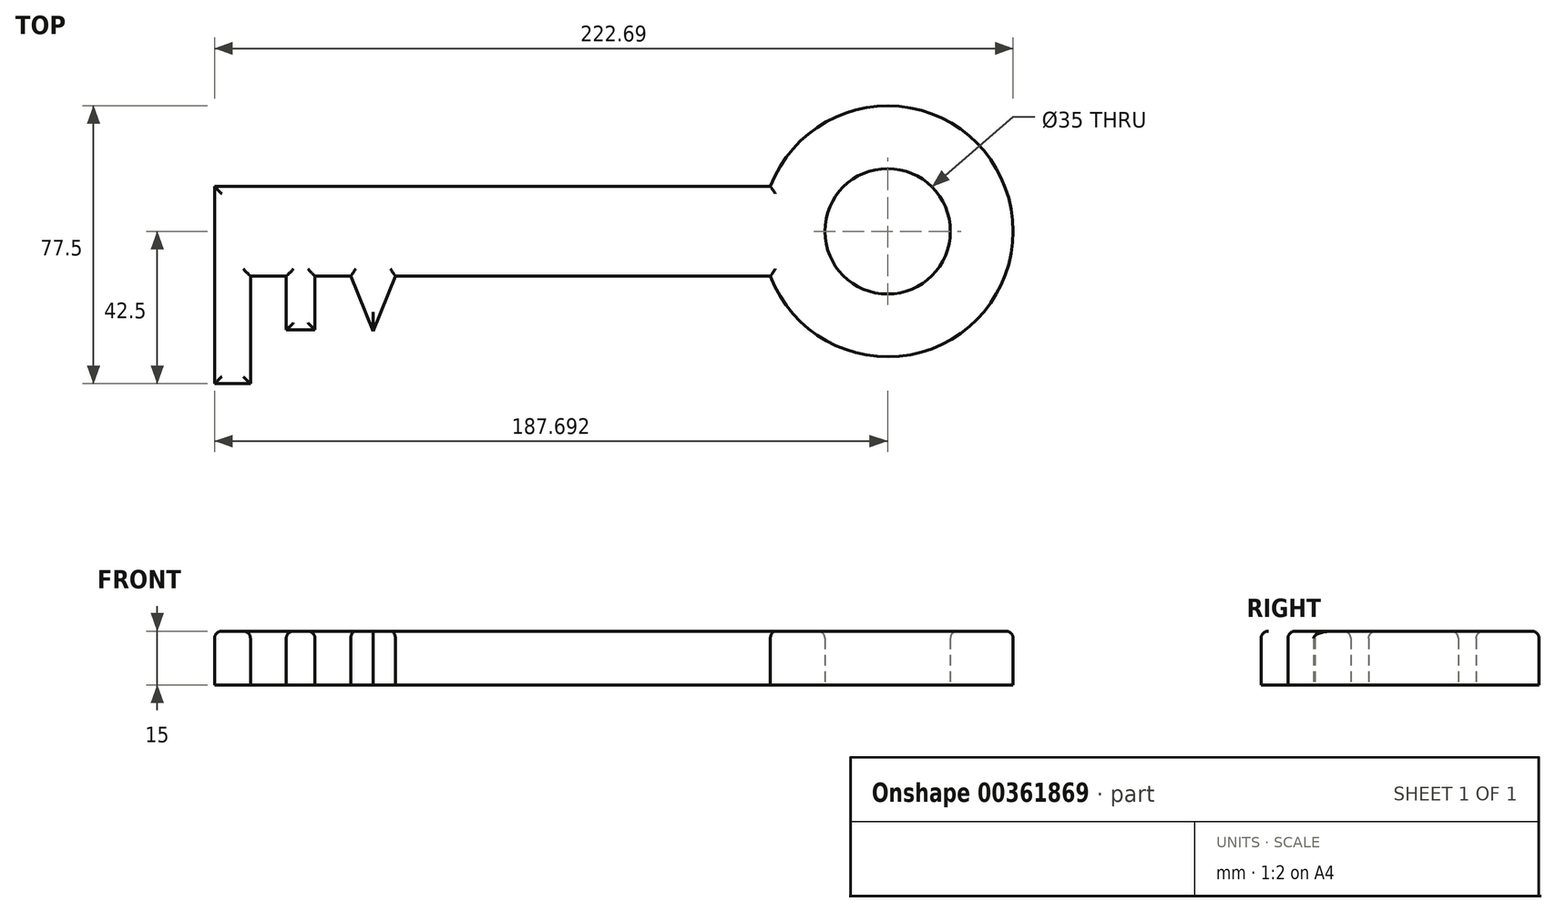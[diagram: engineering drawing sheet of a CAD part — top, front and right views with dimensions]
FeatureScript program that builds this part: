
annotation { "Feature Type Name" : "Feature", "Feature Type Description" : "" }
export const myFeature = defineFeature(function(context is Context, id is Id, definition is map)
    precondition{}
    {
        {
            var Q0;
            Q0=qCreatedBy(makeId("Top.planeOp"),FACE);
            var sketch = newSketch(context, id + "F0", { "sketchPlane" : qUnion([Q0])});
            skLineSegment(sketch, "E0.bottom", {"start": v(-84.95, 32.85) * mm, "end": v(70.05, 32.85) * mm});
            skLineSegment(sketch, "E0.top", {"start": v(-84.95, 7.85) * mm, "end": v(70.05, 7.85) * mm});
            skLineSegment(sketch, "E0.left", {"start": v(-84.95, 32.85) * mm, "end": v(-84.95, 7.85) * mm});
            skLineSegment(sketch, "E0.right", {"start": v(70.05, 32.85) * mm, "end": v(70.05, 7.85) * mm});
            skLineSegment(sketch, "E1.bottom", {"start": v(-84.95, 7.85) * mm, "end": v(-74.95, 7.85) * mm});
            skLineSegment(sketch, "E1.top", {"start": v(-84.95, -22.15) * mm, "end": v(-74.95, -22.15) * mm});
            skLineSegment(sketch, "E1.left", {"start": v(-84.95, 7.85) * mm, "end": v(-84.95, -22.15) * mm});
            skLineSegment(sketch, "E1.right", {"start": v(-74.95, 7.85) * mm, "end": v(-74.95, -22.15) * mm});
            skLineSegment(sketch, "E2.bottom", {"start": v(-64.95, 7.85) * mm, "end": v(-56.95, 7.85) * mm});
            skLineSegment(sketch, "E2.top", {"start": v(-64.95, -7.15) * mm, "end": v(-56.95, -7.15) * mm});
            skLineSegment(sketch, "E2.left", {"start": v(-64.95, 7.85) * mm, "end": v(-64.95, -7.15) * mm});
            skLineSegment(sketch, "E2.right", {"start": v(-56.95, 7.85) * mm, "end": v(-56.95, -7.15) * mm});
            skPoint(sketch, "E3", {"position": v(-46.95, 7.85) * mm});
            skPoint(sketch, "E4", {"position": v(-34.52, 7.85) * mm});
            skPoint(sketch, "E5", {"position": v(-40.74, -7.5) * mm});
            skLineSegment(sketch, "E6", {"start": v(-46.95, 7.85) * mm, "end": v(-40.74, -7.5) * mm});
            skLineSegment(sketch, "E7", {"start": v(-40.74, -7.5) * mm, "end": v(-34.52, 7.85) * mm});
            skArc(sketch, "E8", {"start": v(70.05, 7.85) * mm, "mid": v(137.74, 20.35) * mm, "end": v(70.05, 32.85) * mm});
            skCircle(sketch, "E9", {"center": v(102.74, 20.35) * mm, "radius": 17.5 * mm});
            skLineSegment(sketch, "E10", {"start": v(102.74, 20.35) * mm, "end": v(-84.95, 20.35) * mm, "construction": true});
            skSolve(sketch);
        }
        {
            var Q0;
            Q0 = qSketchRegion(id + "F0", true);
            extrude(context, id + "F1", {"entities" : qUnion([Q0]), "depth" : 15 * mm});
        }
        {
            var Q0;
            Q0=makeQuery(id+"F1.opExtrude","CAP_FACE",FACE,{"disambiguationData":[OSD([sQuery(id+"F0.wireOp",EDGE,"E0.bottom"),sQuery(id+"F0.wireOp",EDGE,"E0.top"),sQuery(id+"F0.wireOp",EDGE,"E0.left"),sQuery(id+"F0.wireOp",EDGE,"E1.top"),sQuery(id+"F0.wireOp",EDGE,"E1.left"),sQuery(id+"F0.wireOp",EDGE,"E1.right"),sQuery(id+"F0.wireOp",EDGE,"E2.top"),sQuery(id+"F0.wireOp",EDGE,"E2.left"),sQuery(id+"F0.wireOp",EDGE,"E2.right"),sQuery(id+"F0.wireOp",EDGE,"E6"),sQuery(id+"F0.wireOp",EDGE,"E7"),sQuery(id+"F0.wireOp",EDGE,"E8"),sQuery(id+"F0.wireOp",EDGE,"E9")])],"isStart":false});
            fillet(context, id + "F2", {"entities" : qUnion([Q0]), "radius" : 2 * mm, "tangentPropagation" : true, "allowEdgeOverflow" : false});
        }
    });
